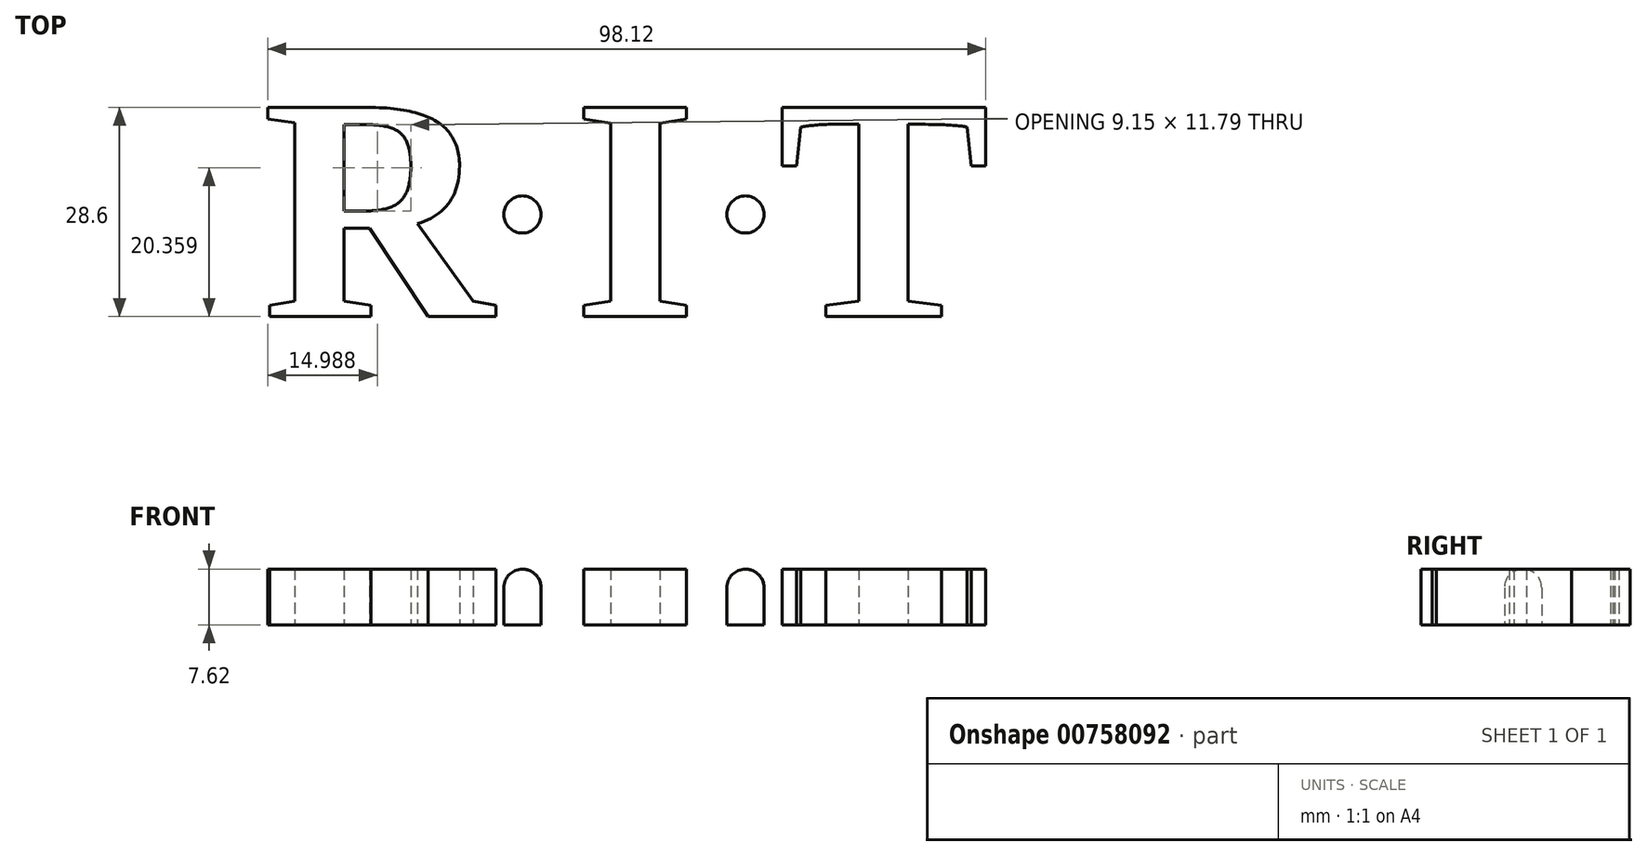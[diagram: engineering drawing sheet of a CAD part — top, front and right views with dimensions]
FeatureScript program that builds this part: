
annotation { "Feature Type Name" : "Feature", "Feature Type Description" : "" }
export const myFeature = defineFeature(function(context is Context, id is Id, definition is map)
    precondition{}
    {
        {
            var Q0;
            Q0=qCreatedBy(makeId("Top.planeOp"),FACE);
            var sketch = newSketch(context, id + "F0", { "sketchPlane" : qUnion([Q0])});
            skText(sketch, "E0", { "text": "R I T", "fontName": "Tinos-Bold.ttf"});
            skCircle(sketch, "E1", {"center": v(35.56, -17.48) * mm, "radius": 2.54 * mm});
            skPoint(sketch, "E2.centerSnap0", {"position": v(50.8, -15.73) * mm});
            skCircle(sketch, "E3", {"center": v(66.04, -17.48) * mm, "radius": 2.54 * mm});
            const initialGuessF0  = {"E0": [0, -0.03145, 1, 0, 0.03145]};
            skSetInitialGuess(sketch, initialGuessF0);
            skSolve(sketch);
        }
        {
            var Q0;
            Q0 = qSketchRegion(id + "F0", true);
            extrude(context, id + "F1", {"entities" : qUnion([Q0]), "depth" : 7.62 * mm, "offsetDistance" : 25.4 * mm});
        }
        {
            var Q0;
            Q0=makeQuery(id+"F1.opExtrude","CAP_FACE",FACE,{"disambiguationData":[OSD([sQuery(id+"F0.wireOp",EDGE,"E1")])],"isStart":false});
            var Q1;
            Q1=makeQuery(id+"F1.opExtrude","CAP_EDGE",EDGE,{"disambiguationData":[OSD([sQuery(id+"F0.wireOp",EDGE,"E3")])],"isStart":false});
            fillet(context, id + "F2", {"entities" : qUnion([Q0, Q1]), "radius" : 2.54 * mm, "tangentPropagation" : true, "allowEdgeOverflow" : false});
        }
    });
